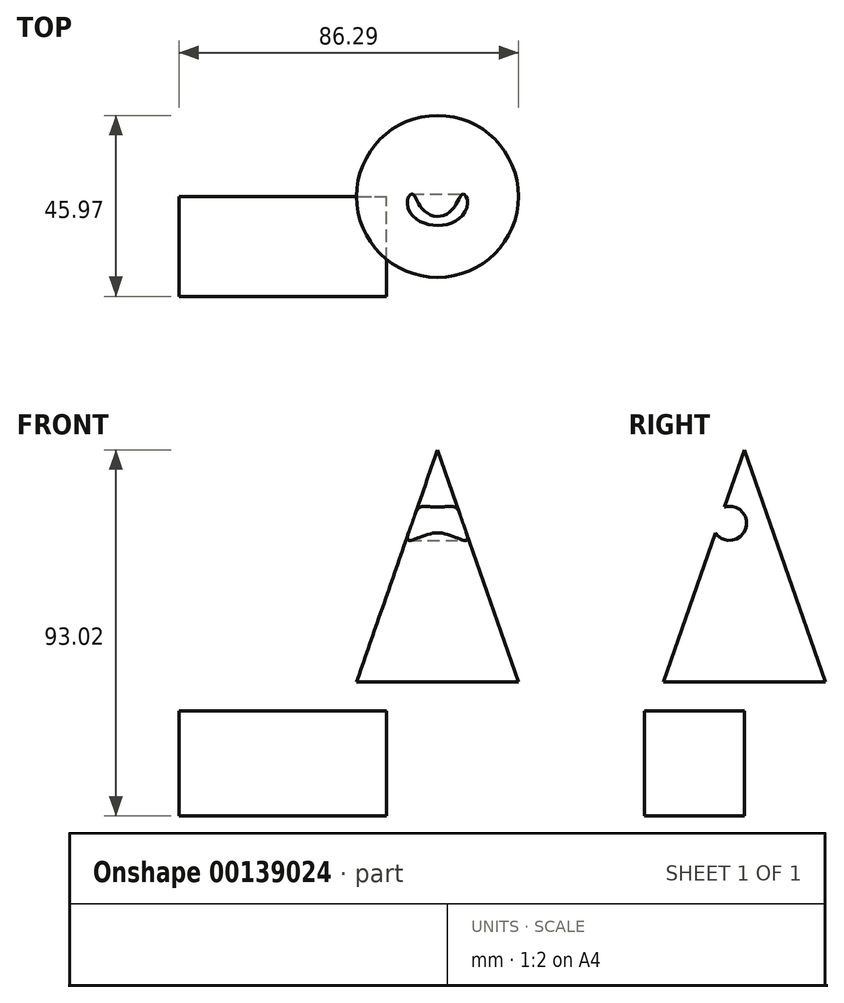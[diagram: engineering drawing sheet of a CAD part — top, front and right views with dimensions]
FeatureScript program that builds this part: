
annotation { "Feature Type Name" : "Feature", "Feature Type Description" : "" }
export const myFeature = defineFeature(function(context is Context, id is Id, definition is map)
    precondition{}
    {
        {
            var Q0;
            Q0=qCreatedBy(makeId("Front.planeOp"),FACE);
            var sketch = newSketch(context, id + "F0", { "sketchPlane" : qUnion([Q0])});
            skLineSegment(sketch, "E0", {"start": v(0, 58.9) * mm, "end": v(8.59, 34.3) * mm});
            skLineSegment(sketch, "E1", {"start": v(20.57, 0) * mm, "end": v(0, 0) * mm});
            skLineSegment(sketch, "E2", {"start": v(0, 0) * mm, "end": v(0, 58.9) * mm});
            skLineSegment(sketch, "E3.trimOffspring", {"start": v(11.98, 24.58) * mm, "end": v(20.57, 0) * mm});
            skPoint(sketch, "E4.center.orphan", {"position": v(10.29, 29.45) * mm});
            skLineSegment(sketch, "E5", {"start": v(8.59, 34.3) * mm, "end": v(11.98, 24.58) * mm});
            skSolve(sketch);
        }
        {
            var Q0;
            Q0=qCreatedBy(makeId("Front.planeOp"),FACE);
            var sketch = newSketch(context, id + "F1", { "sketchPlane" : qUnion([Q0])});
            skLineSegment(sketch, "E6.bottom", {"start": v(-65.72, -7.37) * mm, "end": v(-12.93, -7.37) * mm});
            skLineSegment(sketch, "E6.top", {"start": v(-65.72, -34.13) * mm, "end": v(-12.93, -34.13) * mm});
            skLineSegment(sketch, "E6.left", {"start": v(-65.72, -7.37) * mm, "end": v(-65.72, -34.13) * mm});
            skLineSegment(sketch, "E6.right", {"start": v(-12.93, -7.37) * mm, "end": v(-12.93, -34.13) * mm});
            skSolve(sketch);
        }
        {
            var Q0;
            Q0=makeQuery(id+"F1.imprint","IMPRINT",FACE,{"disambiguationData":[TD([[makeQuery(id+"F1.imprint","IMPRINT",EDGE,{"derivedFrom":sQuery(id+"F1.wireOp",EDGE,"E6.bottom")}),-1.0]])]});
            extrude(context, id + "F2", {"entities" : qUnion([Q0]), "depth" : 25.4 * mm});
        }
        {
            var Q0;
            Q0=makeQuery(id+"F0.imprint","IMPRINT",FACE,{"disambiguationData":[TD([[makeQuery(id+"F0.imprint","IMPRINT",EDGE,{"derivedFrom":sQuery(id+"F0.wireOp",EDGE,"E0")}),-1.0]])]});
            var Q1;
            Q1=sQuery(id+"F0.wireOp",EDGE,"E2");
            revolve(context, id + "F3", {"entities" : qUnion([Q0]), "axis" : qUnion([Q1]), "revolveType" : RevolveType.FULL});
        }
        {
            var Q0;
            Q0=qCreatedBy(makeId("Right.planeOp"),FACE);
            cPlane(context, id + "F4", {"entities" : qUnion([Q0]), "cplaneType" : CPlaneType.OFFSET, "offset" : 11 * mm, "width" : 150 * mm, "height" : 150 * mm});
        }
        {
            var Q0;
            Q0=qCreatedBy(id+"F4.planeOp",FACE);
            var sketch = newSketch(context, id + "F5", { "sketchPlane" : qUnion([Q0])});
            skCircle(sketch, "E7", {"center": v(-3.76, 40.23) * mm, "radius": 4.33 * mm});
            skSolve(sketch);
        }
        {
            var Q0;
            Q0 = qSketchRegion(id + "F5", true);
            extrude(context, id + "F6", {"entities" : qUnion([Q0]), "operationType" : NewBodyOperationType.REMOVE, "oppositeDirection" : true, "depth" : 25 * mm});
        }
    });
